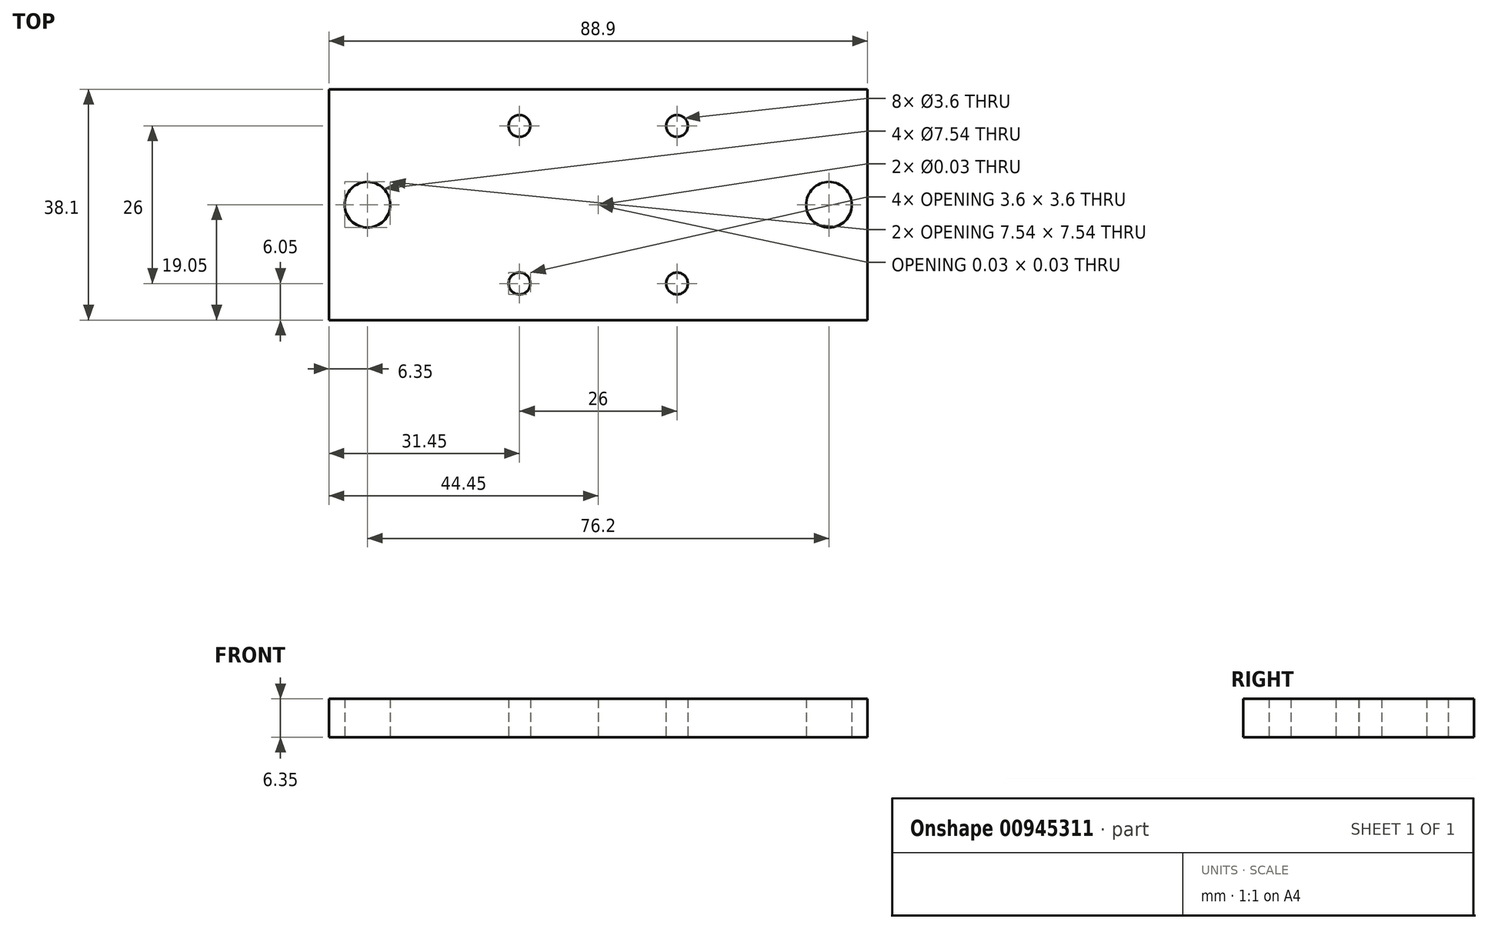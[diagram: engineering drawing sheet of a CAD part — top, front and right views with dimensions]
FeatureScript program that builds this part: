
annotation { "Feature Type Name" : "Feature", "Feature Type Description" : "" }
export const myFeature = defineFeature(function(context is Context, id is Id, definition is map)
    precondition{}
    {
        {
            var Q0;
            Q0=qCreatedBy(makeId("Top.planeOp"),FACE);
            var sketch = newSketch(context, id + "F0", { "sketchPlane" : qUnion([Q0])});
            skLineSegment(sketch, "E0.bottom", {"start": v(44.45, 19.05) * mm, "end": v(-44.45, 19.05) * mm});
            skLineSegment(sketch, "E0.top", {"start": v(44.45, -19.05) * mm, "end": v(-44.45, -19.05) * mm});
            skLineSegment(sketch, "E0.left", {"start": v(44.45, 13) * mm, "end": v(44.45, -19.05) * mm});
            skLineSegment(sketch, "E0.right", {"start": v(-44.45, 19.05) * mm, "end": v(-44.45, -19.05) * mm});
            skPoint(sketch, "E0.middle", {"position": v(0, 0) * mm});
            skLineSegment(sketch, "E1", {"start": v(-13, 19.05) * mm, "end": v(-13, -19.05) * mm, "construction": true});
            skLineSegment(sketch, "E2", {"start": v(13, 19.05) * mm, "end": v(13, -19.05) * mm, "construction": true});
            skLineSegment(sketch, "E3", {"start": v(-44.45, 13) * mm, "end": v(44.45, 13) * mm, "construction": true});
            skLineSegment(sketch, "E4", {"start": v(-44.45, -13) * mm, "end": v(44.45, -13) * mm, "construction": true});
            skPoint(sketch, "E5", {"position": v(-13, 13) * mm});
            skPoint(sketch, "E6", {"position": v(13, 13) * mm});
            skPoint(sketch, "E7", {"position": v(13, -13) * mm});
            skPoint(sketch, "E8", {"position": v(-13, -13) * mm});
            skPoint(sketch, "E9", {"position": v(-38.1, 0) * mm});
            skPoint(sketch, "E10", {"position": v(38.1, 0) * mm});
            skPoint(sketch, "E11.visualSharp", {"position": v(-44.45, 19.05) * mm});
            skPoint(sketch, "E12.visualSharp", {"position": v(-44.45, -19.05) * mm});
            skPoint(sketch, "E13.visualSharp", {"position": v(44.45, -19.05) * mm});
            skPoint(sketch, "E14.visualSharp", {"position": v(44.45, 19.05) * mm});
            skLineSegment(sketch, "E15", {"start": v(44.45, 13) * mm, "end": v(44.45, 19.05) * mm});
            skSolve(sketch);
        }
        {
            var Q0;
            Q0=makeQuery(id+"F0.imprint","IMPRINT",FACE,{"disambiguationData":[TD([[makeQuery(id+"F0.imprint","IMPRINT",EDGE,{"derivedFrom":sQuery(id+"F0.wireOp",EDGE,"E0.bottom")}),1.0]])]});
            extrude(context, id + "F1", {"entities" : qUnion([Q0]), "depth" : 6.35 * mm, "offsetDistance" : 25.4 * mm});
        }
        {
            var Q0;
            Q0=sQuery(id+"F0.wireOp",VERTEX,"E5");
            var Q1;
            Q1=sQuery(id+"F0.wireOp",VERTEX,"E6");
            var Q2;
            Q2=sQuery(id+"F0.wireOp",VERTEX,"E7");
            var Q3;
            Q3=sQuery(id+"F0.wireOp",VERTEX,"E8");
            var Q4;
            Q4=makeQuery(id+"F1.opExtrude","SWEPT_BODY",BODY,{"disambiguationData":[OSD([sQuery(id+"F0.wireOp",EDGE,"E0.bottom"),sQuery(id+"F0.wireOp",EDGE,"E0.top"),sQuery(id+"F0.wireOp",EDGE,"E0.left"),sQuery(id+"F0.wireOp",EDGE,"E0.right")])]});
            hole(context, id + "F2", {"style" : HoleStyle.SIMPLE, "endStyle" : HoleEndStyle.THROUGH, "oppositeDirection" : true, "standardTappedOrClearance" : lookupTablePath({ "fit" : "Loose", "standard" : "ISO", "size" : "M3", "type" : "Clearance" }), "standardBlindInLast" : lookupTablePath({ "fit" : "Loose", "standard" : "ISO", "engagement" : "75%", "pitch" : "0.5 mm", "size" : "M3", "type" : "Clearance & tapped" }), "holeDiameter" : 3.6 * mm, "majorDiameter" : 12.7 * mm, "isTappedThrough" : true, "tappedDepth" : 10.16 * mm, "tapClearance" : 3, "locations" : qUnion([Q0, Q1, Q2, Q3]), "scope" : qUnion([Q4])});
        }
        {
            var Q0;
            Q0=sQuery(id+"F0.wireOp",VERTEX,"E9");
            var Q1;
            Q1=sQuery(id+"F0.wireOp",VERTEX,"E10");
            var Q2;
            Q2=makeQuery(id+"F1.opExtrude","SWEPT_BODY",BODY,{"disambiguationData":[OSD([sQuery(id+"F0.wireOp",EDGE,"E0.bottom"),sQuery(id+"F0.wireOp",EDGE,"E0.top"),sQuery(id+"F0.wireOp",EDGE,"E0.left"),sQuery(id+"F0.wireOp",EDGE,"E0.right")])]});
            hole(context, id + "F3", {"style" : HoleStyle.SIMPLE, "endStyle" : HoleEndStyle.THROUGH, "oppositeDirection" : true, "standardTappedOrClearance" : lookupTablePath({ "fit" : "Loose (ASME)", "standard" : "ANSI", "size" : "1/4", "type" : "Clearance" }), "standardBlindInLast" : lookupTablePath({ "fit" : "Loose", "standard" : "ANSI", "engagement" : "75%", "pitch" : "20 tpi", "size" : "1/4", "type" : "Clearance & tapped" }), "holeDiameter" : 7.54 * mm, "majorDiameter" : 6.35 * mm, "isTappedThrough" : true, "tappedDepth" : 10.16 * mm, "tapClearance" : 3, "locations" : qUnion([Q0, Q1]), "scope" : qUnion([Q2])});
        }
        {
            var Q0;
            Q0=sQuery(id+"F0.wireOp",VERTEX,"E0.middle");
            var Q1;
            Q1=makeQuery(id+"F1.opExtrude","SWEPT_BODY",BODY,{"disambiguationData":[OSD([sQuery(id+"F0.wireOp",EDGE,"E0.bottom"),sQuery(id+"F0.wireOp",EDGE,"E0.top"),sQuery(id+"F0.wireOp",EDGE,"E0.left"),sQuery(id+"F0.wireOp",EDGE,"E0.right"),sQuery(id+"F0.wireOp",EDGE,"E11.filletArc"),sQuery(id+"F0.wireOp",EDGE,"E12.filletArc"),sQuery(id+"F0.wireOp",EDGE,"E13.filletArc"),sQuery(id+"F0.wireOp",EDGE,"E14.filletArc")])]});
            hole(context, id + "F4", {"style" : HoleStyle.SIMPLE, "endStyle" : HoleEndStyle.THROUGH, "oppositeDirection" : true, "standardTappedOrClearance" : lookupTablePath({ "standard" : "ANSI", "size" : "7/8 (0.88)", "type" : "Drilled" }), "standardBlindInLast" : lookupTablePath({ "standard" : "ANSI", "size" : "7/8 (0.88)", "type" : "Drilled" }), "holeDiameter" : 7 / 203.2 * mm, "majorDiameter" : 6.35 * mm, "isTappedThrough" : true, "tappedDepth" : 10.16 * mm, "tapClearance" : 3, "locations" : qUnion([Q0]), "scope" : qUnion([Q1])});
        }
    });
